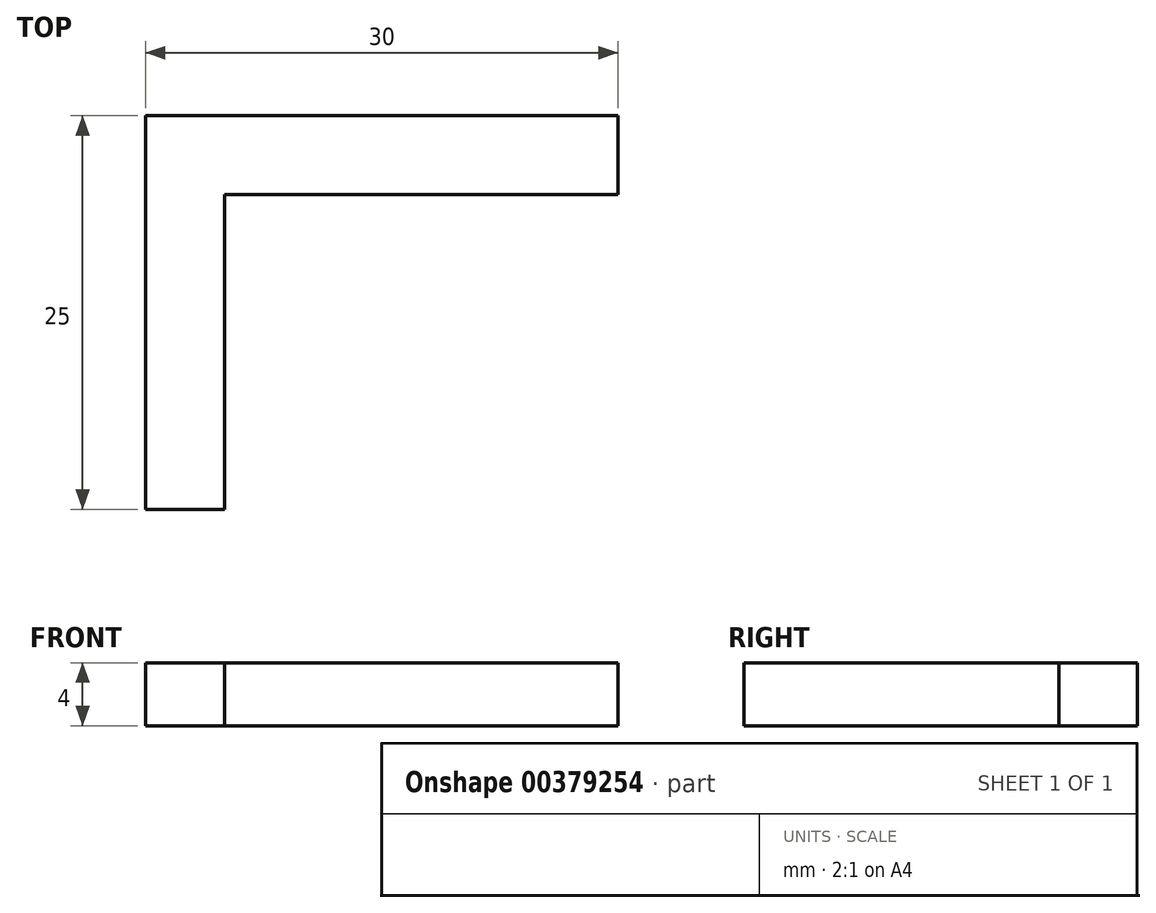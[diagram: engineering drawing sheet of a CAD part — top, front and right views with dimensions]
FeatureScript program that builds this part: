
annotation { "Feature Type Name" : "Feature", "Feature Type Description" : "" }
export const myFeature = defineFeature(function(context is Context, id is Id, definition is map)
    precondition{}
    {
        {
            var Q0;
            Q0=qCreatedBy(makeId("Top.planeOp"),FACE);
            var sketch = newSketch(context, id + "F0", { "sketchPlane" : qUnion([Q0])});
            skLineSegment(sketch, "E0", {"start": v(-5, 0) * mm, "end": v(-5, 25) * mm});
            skLineSegment(sketch, "E1", {"start": v(-5, 25) * mm, "end": v(25, 25) * mm});
            skLineSegment(sketch, "E2", {"start": v(25, 25) * mm, "end": v(25, 20) * mm});
            skLineSegment(sketch, "E3", {"start": v(25, 20) * mm, "end": v(0, 20) * mm});
            skLineSegment(sketch, "E4", {"start": v(0, 20) * mm, "end": v(0, 0) * mm});
            skLineSegment(sketch, "E5", {"start": v(0, 0) * mm, "end": v(-5, 0) * mm});
            skSolve(sketch);
        }
        {
            var Q0;
            Q0 = qSketchRegion(id + "F0", true);
            extrude(context, id + "F1", {"entities" : qUnion([Q0]), "depth" : 4 * mm});
        }
    });
